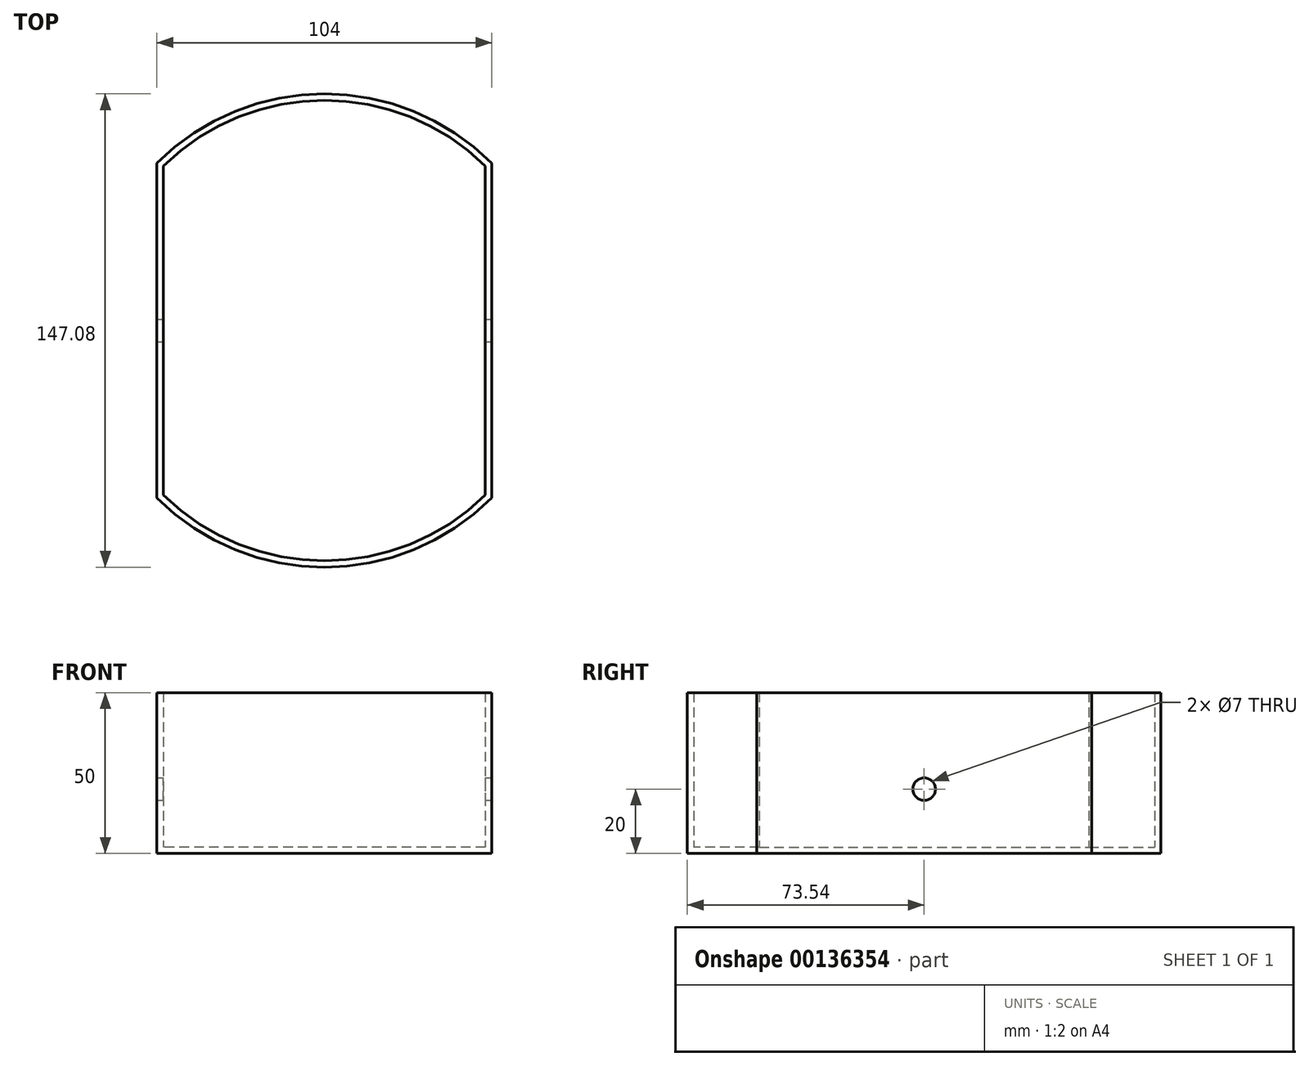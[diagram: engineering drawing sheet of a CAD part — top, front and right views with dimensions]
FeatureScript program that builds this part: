
annotation { "Feature Type Name" : "Feature", "Feature Type Description" : "" }
export const myFeature = defineFeature(function(context is Context, id is Id, definition is map)
    precondition{}
    {
        {
            var Q0;
            Q0=qCreatedBy(makeId("Top.planeOp"),FACE);
            var sketch = newSketch(context, id + "F0", { "sketchPlane" : qUnion([Q0])});
            skCircle(sketch, "E0", {"center": v(0, 0) * mm, "radius": 73.54 * mm});
            skLineSegment(sketch, "E1.bottom", {"start": v(-52, 52) * mm, "end": v(52, 52) * mm});
            skLineSegment(sketch, "E1.top", {"start": v(-52, -52) * mm, "end": v(52, -52) * mm});
            skLineSegment(sketch, "E1.left", {"start": v(-52, 52) * mm, "end": v(-52, -52) * mm});
            skLineSegment(sketch, "E1.right", {"start": v(52, 52) * mm, "end": v(52, -52) * mm});
            skLineSegment(sketch, "E2.bottom", {"start": v(-50, 50) * mm, "end": v(50, 50) * mm});
            skLineSegment(sketch, "E2.top", {"start": v(-50, -50) * mm, "end": v(50, -50) * mm});
            skLineSegment(sketch, "E2.left", {"start": v(-50, 50) * mm, "end": v(-50, -50) * mm});
            skLineSegment(sketch, "E2.right", {"start": v(50, 50) * mm, "end": v(50, -50) * mm});
            skCircle(sketch, "E3", {"center": v(0, 0) * mm, "radius": 71.54 * mm});
            skLineSegment(sketch, "E4", {"start": v(-50, 50) * mm, "end": v(-50, 51.16) * mm});
            skLineSegment(sketch, "E5", {"start": v(50, 50) * mm, "end": v(50, 51.16) * mm});
            skLineSegment(sketch, "E6", {"start": v(50, -50) * mm, "end": v(50, -51.16) * mm});
            skLineSegment(sketch, "E7", {"start": v(-50, -50) * mm, "end": v(-50, -51.16) * mm});
            skSolve(sketch);
        }
        {
            var Q0;
            {var subQ0=sQuery(id+"F0.wireOp",EDGE,"E3");var subQ1=sQuery(id+"F0.wireOp",EDGE,"E1.top");var subQ2=makeQuery(id+"F0.imprint","INTERSECT",VERTEX,{"disambiguationData":[OD(0.0)],"derivedFrom":[subQ1,subQ0]});Q0=makeQuery(id+"F0.imprint","IMPRINT",FACE,{"disambiguationData":[TD([[makeQuery(id+"F0.imprint","IMPRINT",EDGE,{"disambiguationData":[TD([[subQ2,-1.0]])],"derivedFrom":subQ1}),-1.0]])]});}
            var Q1;
            Q1=makeQuery(id+"F0.imprint","IMPRINT",FACE,{"disambiguationData":[TD([[makeQuery(id+"F0.imprint","IMPRINT",EDGE,{"derivedFrom":sQuery(id+"F0.wireOp",EDGE,"E2.bottom")}),-1.0]])]});
            var Q2;
            {var subQ0=sQuery(id+"F0.wireOp",EDGE,"E3");var subQ1=sQuery(id+"F0.wireOp",EDGE,"E1.bottom");var subQ2=makeQuery(id+"F0.imprint","INTERSECT",VERTEX,{"disambiguationData":[OD(0.0)],"derivedFrom":[subQ1,subQ0]});Q2=makeQuery(id+"F0.imprint","IMPRINT",FACE,{"disambiguationData":[TD([[makeQuery(id+"F0.imprint","IMPRINT",EDGE,{"disambiguationData":[TD([[subQ2,-1.0]])],"derivedFrom":subQ1}),1.0]])]});}
            var Q3;
            {var subQ0=sQuery(id+"F0.wireOp",EDGE,"E1.bottom");var subQ4=sQuery(id+"F0.wireOp",EDGE,"E3");var subQ5=makeQuery(id+"F0.imprint","INTERSECT",VERTEX,{"disambiguationData":[OD(0.0)],"derivedFrom":[subQ0,subQ4]});Q3=makeQuery(id+"F0.imprint","IMPRINT",FACE,{"disambiguationData":[TD([[makeQuery(id+"F0.imprint","IMPRINT",EDGE,{"disambiguationData":[TD([[subQ5,1.0]])],"derivedFrom":subQ4}),-1.0]])]});}
            var Q4;
            Q4=makeQuery(id+"F0.imprint","IMPRINT",FACE,{"disambiguationData":[TD([[makeQuery(id+"F0.imprint","IMPRINT",EDGE,{"derivedFrom":sQuery(id+"F0.wireOp",EDGE,"E2.bottom")}),1.0]])]});
            var Q5;
            {var subQ1=sQuery(id+"F0.wireOp",EDGE,"E1.bottom");var subQ3=sQuery(id+"F0.wireOp",EDGE,"E3");var subQ4=makeQuery(id+"F0.imprint","INTERSECT",VERTEX,{"disambiguationData":[OD(0.0)],"derivedFrom":[subQ1,subQ3]});Q5=makeQuery(id+"F0.imprint","IMPRINT",FACE,{"disambiguationData":[TD([[makeQuery(id+"F0.imprint","IMPRINT",EDGE,{"disambiguationData":[TD([[subQ4,-1.0]])],"derivedFrom":subQ3}),-1.0]])]});}
            var Q6;
            {var subQ1=sQuery(id+"F0.wireOp",EDGE,"E1.bottom");var subQ3=sQuery(id+"F0.wireOp",EDGE,"E3");var subQ4=makeQuery(id+"F0.imprint","INTERSECT",VERTEX,{"disambiguationData":[OD(1.0)],"derivedFrom":[subQ1,subQ3]});Q6=makeQuery(id+"F0.imprint","IMPRINT",FACE,{"disambiguationData":[TD([[makeQuery(id+"F0.imprint","IMPRINT",EDGE,{"disambiguationData":[TD([[subQ4,1.0]])],"derivedFrom":subQ3}),-1.0]])]});}
            var Q7;
            {var subQ1=sQuery(id+"F0.wireOp",EDGE,"E1.top");var subQ3=sQuery(id+"F0.wireOp",EDGE,"E3");var subQ4=makeQuery(id+"F0.imprint","INTERSECT",VERTEX,{"disambiguationData":[OD(1.0)],"derivedFrom":[subQ1,subQ3]});Q7=makeQuery(id+"F0.imprint","IMPRINT",FACE,{"disambiguationData":[TD([[makeQuery(id+"F0.imprint","IMPRINT",EDGE,{"disambiguationData":[TD([[subQ4,-1.0]])],"derivedFrom":subQ3}),-1.0]])]});}
            var Q8;
            {var subQ0=sQuery(id+"F0.wireOp",EDGE,"E1.top");var subQ4=sQuery(id+"F0.wireOp",EDGE,"E3");var subQ5=makeQuery(id+"F0.imprint","INTERSECT",VERTEX,{"disambiguationData":[OD(0.0)],"derivedFrom":[subQ0,subQ4]});Q8=makeQuery(id+"F0.imprint","IMPRINT",FACE,{"disambiguationData":[TD([[makeQuery(id+"F0.imprint","IMPRINT",EDGE,{"disambiguationData":[TD([[subQ5,-1.0]])],"derivedFrom":subQ4}),-1.0]])]});}
            var Q9;
            {var subQ1=sQuery(id+"F0.wireOp",EDGE,"E1.top");var subQ3=sQuery(id+"F0.wireOp",EDGE,"E3");var subQ4=makeQuery(id+"F0.imprint","INTERSECT",VERTEX,{"disambiguationData":[OD(0.0)],"derivedFrom":[subQ1,subQ3]});Q9=makeQuery(id+"F0.imprint","IMPRINT",FACE,{"disambiguationData":[TD([[makeQuery(id+"F0.imprint","IMPRINT",EDGE,{"disambiguationData":[TD([[subQ4,1.0]])],"derivedFrom":subQ3}),-1.0]])]});}
            var Q10;
            Q10=makeQuery(id+"F0.imprint","IMPRINT",FACE,{"disambiguationData":[TD([[makeQuery(id+"F0.imprint","IMPRINT",EDGE,{"derivedFrom":sQuery(id+"F0.wireOp",EDGE,"E2.left")}),-1.0]])]});
            var Q11;
            Q11=makeQuery(id+"F0.imprint","IMPRINT",FACE,{"disambiguationData":[TD([[makeQuery(id+"F0.imprint","IMPRINT",EDGE,{"derivedFrom":sQuery(id+"F0.wireOp",EDGE,"E2.right")}),1.0]])]});
            var Q12;
            Q12=makeQuery(id+"F0.imprint","IMPRINT",FACE,{"disambiguationData":[TD([[makeQuery(id+"F0.imprint","IMPRINT",EDGE,{"derivedFrom":sQuery(id+"F0.wireOp",EDGE,"E2.top")}),-1.0]])]});
            extrude(context, id + "F1", {"entities" : qUnion([Q0, Q1, Q2, Q3, Q4, Q5, Q6, Q7, Q8, Q9, Q10, Q11, Q12]), "depth" : 2 * mm});
        }
        {
            var Q0;
            Q0=makeQuery(id+"F0.imprint","IMPRINT",FACE,{"disambiguationData":[TD([[makeQuery(id+"F0.imprint","IMPRINT",EDGE,{"derivedFrom":sQuery(id+"F0.wireOp",EDGE,"E2.left")}),-1.0]])]});
            var Q1;
            {var subQ3=sQuery(id+"F0.wireOp",EDGE,"E3");var subQ6=makeQuery(id+"F0.imprint","INTERSECT",VERTEX,{"derivedFrom":[subQ3,sQuery(id+"F0.wireOp",EDGE,"E4")]});Q1=makeQuery(id+"F0.imprint","IMPRINT",FACE,{"disambiguationData":[TD([[makeQuery(id+"F0.imprint","IMPRINT",EDGE,{"disambiguationData":[TD([[subQ6,1.0]])],"derivedFrom":subQ3}),-1.0]])]});}
            var Q2;
            {var subQ0=sQuery(id+"F0.wireOp",EDGE,"E1.bottom");var subQ4=sQuery(id+"F0.wireOp",EDGE,"E3");var subQ5=makeQuery(id+"F0.imprint","INTERSECT",VERTEX,{"disambiguationData":[OD(0.0)],"derivedFrom":[subQ0,subQ4]});Q2=makeQuery(id+"F0.imprint","IMPRINT",FACE,{"disambiguationData":[TD([[makeQuery(id+"F0.imprint","IMPRINT",EDGE,{"disambiguationData":[TD([[subQ5,1.0]])],"derivedFrom":subQ4}),-1.0]])]});}
            var Q3;
            Q3=makeQuery(id+"F0.imprint","IMPRINT",FACE,{"disambiguationData":[TD([[makeQuery(id+"F0.imprint","IMPRINT",EDGE,{"derivedFrom":sQuery(id+"F0.wireOp",EDGE,"E2.right")}),1.0]])]});
            var Q4;
            {var subQ3=sQuery(id+"F0.wireOp",EDGE,"E3");var subQ5=makeQuery(id+"F0.imprint","INTERSECT",VERTEX,{"derivedFrom":[subQ3,sQuery(id+"F0.wireOp",EDGE,"E5")]});Q4=makeQuery(id+"F0.imprint","IMPRINT",FACE,{"disambiguationData":[TD([[makeQuery(id+"F0.imprint","IMPRINT",EDGE,{"disambiguationData":[TD([[subQ5,1.0]])],"derivedFrom":subQ3}),-1.0]])]});}
            var Q5;
            {var subQ3=sQuery(id+"F0.wireOp",EDGE,"E3");var subQ6=makeQuery(id+"F0.imprint","INTERSECT",VERTEX,{"derivedFrom":[subQ3,sQuery(id+"F0.wireOp",EDGE,"E6")]});Q5=makeQuery(id+"F0.imprint","IMPRINT",FACE,{"disambiguationData":[TD([[makeQuery(id+"F0.imprint","IMPRINT",EDGE,{"disambiguationData":[TD([[subQ6,1.0]])],"derivedFrom":subQ3}),-1.0]])]});}
            var Q6;
            {var subQ0=sQuery(id+"F0.wireOp",EDGE,"E1.top");var subQ4=sQuery(id+"F0.wireOp",EDGE,"E3");var subQ5=makeQuery(id+"F0.imprint","INTERSECT",VERTEX,{"disambiguationData":[OD(0.0)],"derivedFrom":[subQ0,subQ4]});Q6=makeQuery(id+"F0.imprint","IMPRINT",FACE,{"disambiguationData":[TD([[makeQuery(id+"F0.imprint","IMPRINT",EDGE,{"disambiguationData":[TD([[subQ5,-1.0]])],"derivedFrom":subQ4}),-1.0]])]});}
            var Q7;
            {var subQ3=sQuery(id+"F0.wireOp",EDGE,"E3");var subQ6=makeQuery(id+"F0.imprint","INTERSECT",VERTEX,{"derivedFrom":[subQ3,sQuery(id+"F0.wireOp",EDGE,"E7")]});Q7=makeQuery(id+"F0.imprint","IMPRINT",FACE,{"disambiguationData":[TD([[makeQuery(id+"F0.imprint","IMPRINT",EDGE,{"disambiguationData":[TD([[subQ6,1.0]])],"derivedFrom":subQ3}),-1.0]])]});}
            extrude(context, id + "F2", {"entities" : qUnion([Q0, Q1, Q2, Q3, Q4, Q5, Q6, Q7]), "operationType" : NewBodyOperationType.ADD, "depth" : 50 * mm});
        }
        {
            var Q0;
            {var subQ0=sQuery(id+"F0.wireOp",EDGE,"E1.right");Q0=makeQuery(id+"F2.boolean.opBoolean","MERGE",FACE,{"derivedFrom":[makeQuery(id+"F1.opExtrude","SWEPT_FACE",FACE,{"disambiguationData":[OSD([subQ0])]}),makeQuery(id+"F2.opExtrude","SWEPT_FACE",FACE,{"disambiguationData":[OSD([subQ0])]})]});}
            var sketch = newSketch(context, id + "F3", { "sketchPlane" : qUnion([Q0])});
            skLineSegment(sketch, "E8", {"start": v(0, 0) * mm, "end": v(0, 50) * mm, "construction": true});
            skCircle(sketch, "E9", {"center": v(0, 20) * mm, "radius": 35 * mm});
            skCircle(sketch, "E10", {"center": v(0, 20) * mm, "radius": 3.5 * mm});
            skSolve(sketch);
        }
        {
            var Q0;
            Q0=makeQuery(id+"F3.imprint","IMPRINT",FACE,{"disambiguationData":[TD([[makeQuery(id+"F3.imprint","IMPRINT",EDGE,{"derivedFrom":sQuery(id+"F3.wireOp",EDGE,"E10")}),1.0]])]});
            extrude(context, id + "F4", {"entities" : qUnion([Q0]), "operationType" : NewBodyOperationType.REMOVE, "endBound" : BoundingType.THROUGH_ALL, "oppositeDirection" : true, "depth" : 25 * mm});
        }
    });
